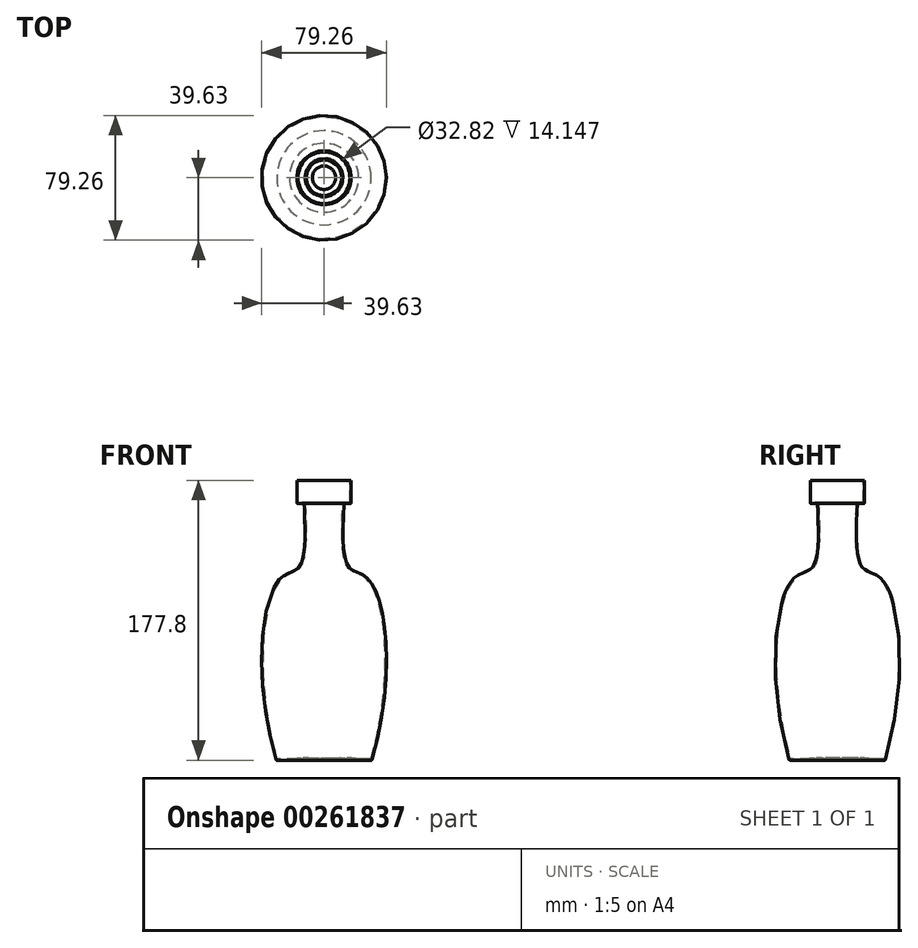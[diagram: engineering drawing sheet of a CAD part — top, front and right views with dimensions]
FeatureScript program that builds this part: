
annotation { "Feature Type Name" : "Feature", "Feature Type Description" : "" }
export const myFeature = defineFeature(function(context is Context, id is Id, definition is map)
    precondition{}
    {
        {
            var Q0;
            Q0=qCreatedBy(makeId("Front.planeOp"),FACE);
            var sketch = newSketch(context, id + "F0", { "sketchPlane" : qUnion([Q0])});
            skLineSegment(sketch, "E0", {"start": v(0, 82.89) * mm, "end": v(0, -94.91) * mm});
            skLineSegment(sketch, "E1", {"start": v(0, -94.91) * mm, "end": v(-30.48, -94.91) * mm, "construction": true});
            skFitSpline(sketch, "E2", {"points": [v(-30.48, -94.91) * mm, v(-27.81, 20.51) * mm, v(-16.36, 27.06) * mm, v(-12.67, 67.98) * mm], "startDerivative": vector(-89.67, 313.9) * mm, "endDerivative": vector(-8.7, 196.96) * mm});
            skLineSegment(sketch, "E3", {"start": v(-12.67, 67.98) * mm, "end": v(-17.17, 67.98) * mm});
            skLineSegment(sketch, "E4", {"start": v(-17.17, 67.98) * mm, "end": v(-17.17, 82.89) * mm});
            skLineSegment(sketch, "E5", {"start": v(-17.17, 82.89) * mm, "end": v(0, 82.89) * mm});
            skLineSegment(sketch, "E6", {"start": v(-30.48, -94.91) * mm, "end": v(-21.9, -94.91) * mm});
            skLineSegment(sketch, "E7", {"start": v(0, -94.91) * mm, "end": v(-7.51, -94.91) * mm});
            skFitSpline(sketch, "E8", {"points": [v(-21.9, -94.91) * mm, v(-16.66, -94.3) * mm, v(-11.59, -94.19) * mm, v(-7.51, -94.91) * mm], "startDerivative": vector(14.96, 1.96) * mm, "endDerivative": vector(12.78, -2.95) * mm});
            skSolve(sketch);
        }
        {
            var Q0;
            Q0=makeQuery(id+"F0.imprint","IMPRINT",FACE,{"disambiguationData":[TD([[makeQuery(id+"F0.imprint","IMPRINT",EDGE,{"derivedFrom":sQuery(id+"F0.wireOp",EDGE,"E0")}),-1.0]])]});
            var Q1;
            Q1=sQuery(id+"F0.wireOp",EDGE,"E0");
            revolve(context, id + "F1", {"entities" : qUnion([Q0]), "axis" : qUnion([Q1]), "revolveType" : RevolveType.FULL});
        }
        {
            var Q0;
            Q0=makeQuery(id+"F1.opRevolve","SWEPT_FACE",FACE,{"disambiguationData":[OSD([sQuery(id+"F0.wireOp",EDGE,"E5")])]});
            shell(context, id + "F2", {"entities" : qUnion([Q0]), "thickness" : 0.76 * mm});
        }
        {
            var Q0;
            Q0=makeQuery(id+"F1.opRevolve","SWEPT_EDGE",EDGE,{"disambiguationData":[OSD([sQuery(id+"F0.wireOp",EDGE,"E3"),sQuery(id+"F0.wireOp",EDGE,"E4")])]});
            fillet(context, id + "F3", {"entities" : qUnion([Q0]), "radius" : 0.5 * mm, "tangentPropagation" : true, "allowEdgeOverflow" : false});
        }
        {
            var Q0;
            Q0=makeQuery(id+"F1.opRevolve","SWEPT_EDGE",EDGE,{"disambiguationData":[OSD([sQuery(id+"F0.wireOp",EDGE,"E2"),sQuery(id+"F0.wireOp",EDGE,"E6")])]});
            fillet(context, id + "F4", {"entities" : qUnion([Q0]), "radius" : 0.5 * mm, "tangentPropagation" : true, "allowEdgeOverflow" : false});
        }
    });
